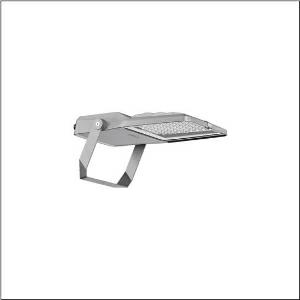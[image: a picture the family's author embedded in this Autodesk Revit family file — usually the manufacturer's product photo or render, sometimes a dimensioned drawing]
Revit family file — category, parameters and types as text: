
# Revit family: floodlight_fl_21_mini___pl61_5xa7776d2c1a_dc0d
name_source: partatom
category: Lighting Fixtures
units: mm (PartAtom-declared; Revit-internal decimal feet)

## family parameters
Cut with Voids When Loaded = No
Host = Face
Light Source = No
Part Type = Normal
Room Calculation Point = No
Round Connector Dimension = Use Diameter
Shared = No

## types (1)
- --- (1 x LED, 17510 lm, 142.9 W, 3000K)
    Apparent Load = 143 VA
    CIE Flux Codes = 33 65 98 100 100
    Color Rendering = 70
    Color Temperature = 3000K
    Default Elevation = 1800 mm
    Description = Floodlight FL 21 mini, floodlight, primary light control with lens, of PMMA, primary optical cover: protective disc, of toughened safety glass, transparent, light distribution: PL61, light emission: direct distribution, installation type: surface-mounted, LED, High Power LED, rated luminous flux: 17.510lm, luminous efficacy: 123lm/W, light colour: 730, colour temperature: 3000K, control gear: Smart Interface (Zhaga), control: flexible luminous flux parameterisation, time-dependent luminous flux control, constant luminous flux control, overheat protection, pre-setting: logarithmic dimming characteristic, with terminal, 6-pole, mains connection: 220..240V, AC, 50/60Hz, start of lifetime: 143W, end of service life: 151W, reduction: 63W, luminaire housing, of diecast aluminium, powder-coated, Siteco® metallic grey (DB 702S), corrosivity category C5 mid according to DIN EN ISO 12944, suitable for swimming pools, chlorine-resistant, sealing non-destructively replaceable, mounting bracket, of steel, galvanised, powder-coated, Siteco® metallic grey (DB 702S), Smart Interface below and above, protection rating (complete): IP66, insulation class (complete): insulation class II (safety insulation), certification: CE, ENEC, VDE, protection symbol: D, impact resistance: IK08, permissible operating ambient temperature: -40..+40°C, permissible operating ambient temperature for outdoor applications: -40..+50°C, standard: DIN EN 12944, LABS conformity tested according to VDMA 24364:2018-05, packaging unit: 1 piece

Light Distribution: PL61
    Height = 70 mm
    Lamp = 1 x LED
    Lamp Light Flux = 17510 lm
    Lamp Power = 142.9 W
    Lamp count = 1
    Length = 485 mm
    Luminous efficacy = 123 lm/W
    Manufacturer = Siteco
    ModVariant = No
    Model = 5XA7776D2C1A
    Number of Poles = 1
    OnlyDefault = Yes
    Power Factor = 1
    Product Name = Floodlight FL 21 mini | PL61
    Product group = floodlight | pylon annexe
    ProductGroupID = 6200
    Protection Class = Protection class II
    Protection Degree = IP 66
    RLX_Detail_Level = 1
    RLX_Emergency_Light_Flux = 0 lm
    RLX_Emergency_Type = 0
    RLX_Emergency_Type_DB = No
    RlxData = <blob elided: 96329 chars, md5=75d08ff6>
    Socket = socket
    Standby Power = 0 W
    System Light Flux = 17510 lm
    System Power = 143 W
    Type Comments = factory setting: luminous flux: 100 % | dim-lin: 254 | 730 mA
    Type Image = l_1006845.jpg
    URL = http://relux.com
    VarID = @adj_171890
    Voltage = 0 V
    Weight = 0.00 kg
    Width = 337 mm

## geometry (parser evidence)
native form markers: Blend x4, Sweep x11
no freeform markers — native parametric forms only
